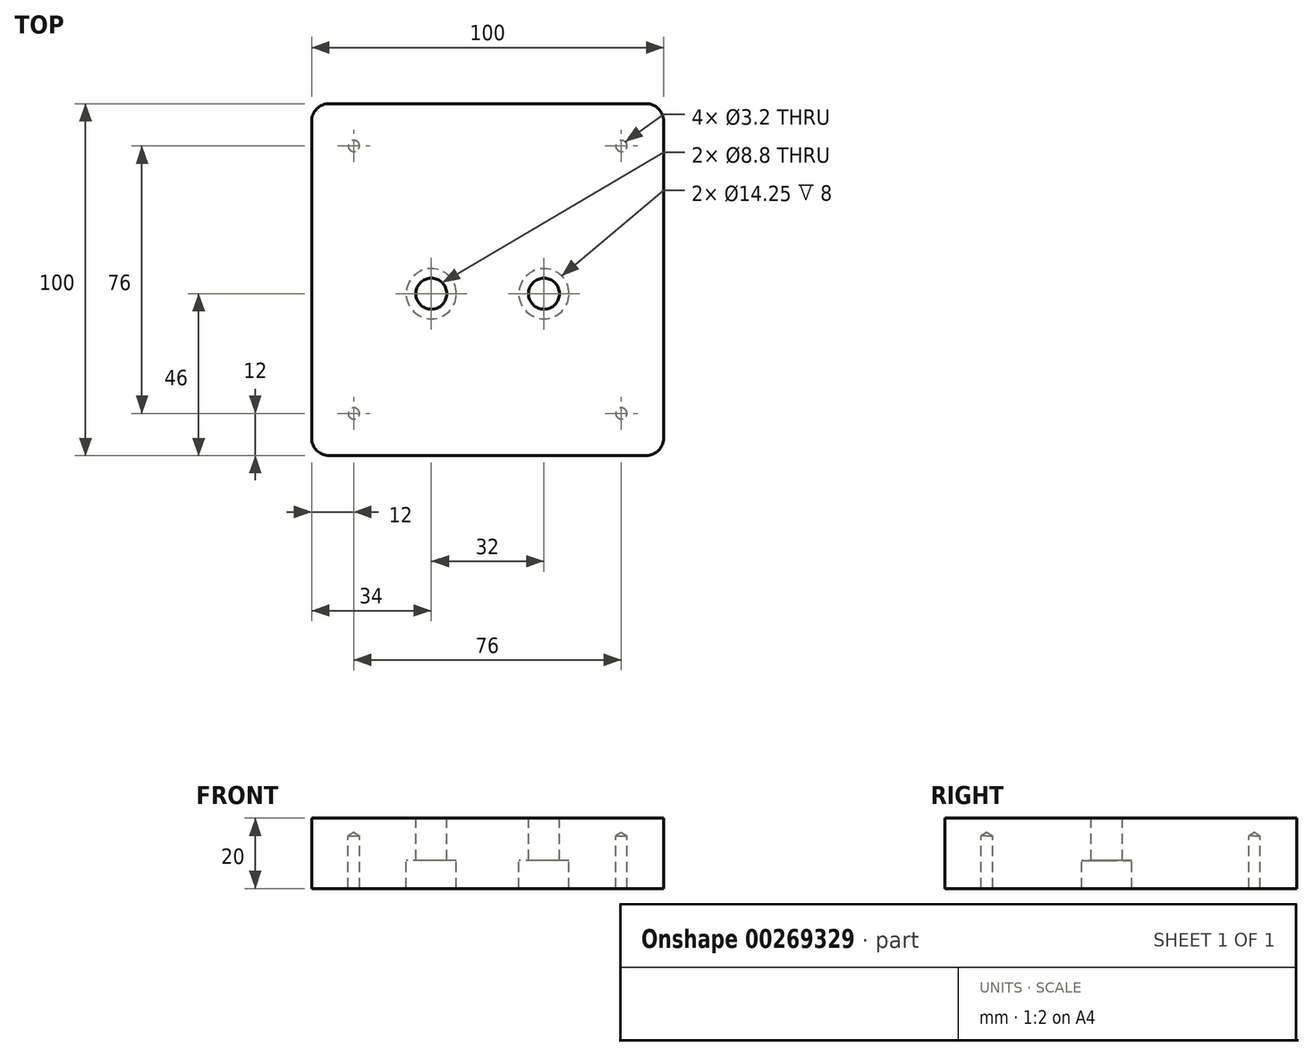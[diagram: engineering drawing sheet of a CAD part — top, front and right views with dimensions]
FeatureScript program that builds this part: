
annotation { "Feature Type Name" : "Feature", "Feature Type Description" : "" }
export const myFeature = defineFeature(function(context is Context, id is Id, definition is map)
    precondition{}
    {
        {
            var Q0;
            Q0=qCreatedBy(makeId("Top.planeOp"),FACE);
            var sketch = newSketch(context, id + "F0", { "sketchPlane" : qUnion([Q0])});
            skLineSegment(sketch, "E0.bottom", {"start": v(-45, -50) * mm, "end": v(45, -50) * mm});
            skLineSegment(sketch, "E0.top", {"start": v(-45, 50) * mm, "end": v(45, 50) * mm});
            skLineSegment(sketch, "E0.left", {"start": v(-50, -45) * mm, "end": v(-50, 45) * mm});
            skLineSegment(sketch, "E0.right", {"start": v(50, -45) * mm, "end": v(50, 45) * mm});
            skPoint(sketch, "E0.middle", {"position": v(0, 0) * mm});
            skPoint(sketch, "E1.visualSharp", {"position": v(-50, 50) * mm});
            skArc(sketch, "E1.filletArc", {"start": v(-45, 50) * mm, "mid": v(-48.54, 48.54) * mm, "end": v(-50, 45) * mm});
            skPoint(sketch, "E2.visualSharp", {"position": v(50, 50) * mm});
            skArc(sketch, "E2.filletArc", {"start": v(50, 45) * mm, "mid": v(48.54, 48.54) * mm, "end": v(45, 50) * mm});
            skPoint(sketch, "E3.visualSharp", {"position": v(50, -50) * mm});
            skArc(sketch, "E3.filletArc", {"start": v(45, -50) * mm, "mid": v(48.54, -48.54) * mm, "end": v(50, -45) * mm});
            skPoint(sketch, "E4.visualSharp", {"position": v(-50, -50) * mm});
            skArc(sketch, "E4.filletArc", {"start": v(-50, -45) * mm, "mid": v(-48.54, -48.54) * mm, "end": v(-45, -50) * mm});
            skSolve(sketch);
        }
        {
            var Q0;
            Q0=makeQuery(id+"F0.imprint","IMPRINT",FACE,{"disambiguationData":[TD([[makeQuery(id+"F0.imprint","IMPRINT",EDGE,{"derivedFrom":sQuery(id+"F0.wireOp",EDGE,"E0.bottom")}),1.0]])]});
            var Q1;
            Q1=sQuery(id+"F0.wireOp",EDGE,"E0.top");
            var Q2;
            Q2=sQuery(id+"F0.wireOp",EDGE,"E1.filletArc");
            var Q3;
            Q3=sQuery(id+"F0.wireOp",EDGE,"E4.filletArc");
            var Q4;
            Q4=sQuery(id+"F0.wireOp",EDGE,"E0.left");
            var Q5;
            Q5=sQuery(id+"F0.wireOp",EDGE,"E0.bottom");
            var Q6;
            Q6=sQuery(id+"F0.wireOp",EDGE,"E3.filletArc");
            var Q7;
            Q7=sQuery(id+"F0.wireOp",EDGE,"E0.right");
            var Q8;
            Q8=sQuery(id+"F0.wireOp",EDGE,"E2.filletArc");
            extrude(context, id + "F1", {"entities" : qUnion([Q0]), "surfaceEntities" : qUnion([Q1, Q2, Q3, Q4, Q5, Q6, Q7, Q8]), "depth" : 20 * mm});
        }
        {
            var Q0;
            Q0=makeQuery(id+"F1.opExtrude","CAP_FACE",FACE,{"disambiguationData":[OSD([sQuery(id+"F0.wireOp",EDGE,"E0.bottom"),sQuery(id+"F0.wireOp",EDGE,"E0.top"),sQuery(id+"F0.wireOp",EDGE,"E0.left"),sQuery(id+"F0.wireOp",EDGE,"E0.right"),sQuery(id+"F0.wireOp",EDGE,"E1.filletArc"),sQuery(id+"F0.wireOp",EDGE,"E2.filletArc"),sQuery(id+"F0.wireOp",EDGE,"E3.filletArc"),sQuery(id+"F0.wireOp",EDGE,"E4.filletArc"),sQuery(id+"F0.wireOp",EDGE,"TYAgWWRq-5I0c-fqWa-FtLE-zTj06zcV9rhc"),sQuery(id+"F0.wireOp",EDGE,"h0C35NKk-MYir-jIPc-H61i-xjHMarGL54rI")])],"isStart":true});
            var sketch = newSketch(context, id + "F2", { "sketchPlane" : qUnion([Q0])});
            skPoint(sketch, "E5", {"position": v(-16, 4) * mm});
            skPoint(sketch, "E6", {"position": v(16, 4) * mm});
            skLineSegment(sketch, "E7", {"start": v(-50, 4) * mm, "end": v(50, 4) * mm, "construction": true});
            skLineSegment(sketch, "E8", {"start": v(0, 50) * mm, "end": v(0, 4) * mm, "construction": true});
            skSolve(sketch);
        }
        {
            var Q0;
            Q0=sQuery(id+"F2.wireOp",VERTEX,"E5");
            var Q1;
            Q1=sQuery(id+"F2.wireOp",VERTEX,"E6");
            var Q2;
            Q2=makeQuery(id+"F1.opExtrude","SWEPT_BODY",BODY,{"disambiguationData":[OSD([sQuery(id+"F0.wireOp",EDGE,"E0.bottom"),sQuery(id+"F0.wireOp",EDGE,"E0.top"),sQuery(id+"F0.wireOp",EDGE,"E0.left"),sQuery(id+"F0.wireOp",EDGE,"E0.right"),sQuery(id+"F0.wireOp",EDGE,"E1.filletArc"),sQuery(id+"F0.wireOp",EDGE,"E2.filletArc"),sQuery(id+"F0.wireOp",EDGE,"E3.filletArc"),sQuery(id+"F0.wireOp",EDGE,"E4.filletArc"),sQuery(id+"F0.wireOp",EDGE,"TYAgWWRq-5I0c-fqWa-FtLE-zTj06zcV9rhc"),sQuery(id+"F0.wireOp",EDGE,"h0C35NKk-MYir-jIPc-H61i-xjHMarGL54rI")])]});
            hole(context, id + "F3", {"style" : HoleStyle.C_BORE, "endStyle" : HoleEndStyle.THROUGH, "standardTappedOrClearance" : lookupTablePath({ "standard" : "ISO", "fit" : "Normal", "size" : "M8", "type" : "Clearance" }), "standardBlindInLast" : lookupTablePath({ "fit" : "Standard", "standard" : "ISO", "size" : "M8", "type" : "Clearance" }), "holeDiameter" : 8.8 * mm, "cBoreDiameter" : 14.25 * mm, "cBoreDepth" : 8 * mm, "locations" : qUnion([Q0, Q1]), "scope" : qUnion([Q2]), "isTappedThrough" : true});
        }
        {
            var Q0;
            Q0=makeQuery(id+"F1.opExtrude","CAP_FACE",FACE,{"disambiguationData":[OSD([sQuery(id+"F0.wireOp",EDGE,"E0.bottom"),sQuery(id+"F0.wireOp",EDGE,"E0.top"),sQuery(id+"F0.wireOp",EDGE,"E0.left"),sQuery(id+"F0.wireOp",EDGE,"E0.right"),sQuery(id+"F0.wireOp",EDGE,"E1.filletArc"),sQuery(id+"F0.wireOp",EDGE,"E2.filletArc"),sQuery(id+"F0.wireOp",EDGE,"E3.filletArc"),sQuery(id+"F0.wireOp",EDGE,"E4.filletArc")])],"isStart":true});
            var sketch = newSketch(context, id + "F4", { "sketchPlane" : qUnion([Q0])});
            skLineSegment(sketch, "E9", {"start": v(-50, 38) * mm, "end": v(-38, 38) * mm, "construction": true});
            skLineSegment(sketch, "E10", {"start": v(-38, 38) * mm, "end": v(-38, 50) * mm, "construction": true});
            skPoint(sketch, "E11", {"position": v(-38, 38) * mm});
            skPoint(sketch, "E12.1.0", {"position": v(-38, -38) * mm});
            skPoint(sketch, "E12.2.0", {"position": v(38, -38) * mm});
            skPoint(sketch, "E12.3.0", {"position": v(38, 38) * mm});
            skPoint(sketch, "E12.center", {"position": v(0, 0) * mm});
            skSolve(sketch);
        }
        {
            var Q0;
            Q0=sQuery(id+"F4.wireOp",VERTEX,"E11");
            var Q1;
            Q1=sQuery(id+"F4.wireOp",VERTEX,"E12.3.0");
            var Q2;
            Q2=sQuery(id+"F4.wireOp",VERTEX,"E12.2.0");
            var Q3;
            Q3=sQuery(id+"F4.wireOp",VERTEX,"E12.1.0");
            var Q4;
            Q4=makeQuery(id+"F1.opExtrude","SWEPT_BODY",BODY,{"disambiguationData":[OSD([sQuery(id+"F0.wireOp",EDGE,"E0.bottom"),sQuery(id+"F0.wireOp",EDGE,"E0.top"),sQuery(id+"F0.wireOp",EDGE,"E0.left"),sQuery(id+"F0.wireOp",EDGE,"E0.right"),sQuery(id+"F0.wireOp",EDGE,"E1.filletArc"),sQuery(id+"F0.wireOp",EDGE,"E2.filletArc"),sQuery(id+"F0.wireOp",EDGE,"E3.filletArc"),sQuery(id+"F0.wireOp",EDGE,"E4.filletArc")])]});
            hole(context, id + "F5", {"style" : HoleStyle.SIMPLE, "endStyle" : HoleEndStyle.BLIND, "standardTappedOrClearance" : lookupTablePath({ "standard" : "ISO", "engagement" : "75%", "pitch" : "0.75 mm", "size" : "M4", "type" : "Tapped" }), "standardBlindInLast" : lookupTablePath({ "standard" : "ISO", "engagement" : "75%", "pitch" : "0.75 mm", "size" : "M4", "type" : "Tapped" }), "holeDiameter" : 3.2 * mm, "holeDepth" : 15 * mm, "locations" : qUnion([Q0, Q1, Q2, Q3]), "scope" : qUnion([Q4])});
        }
    });
